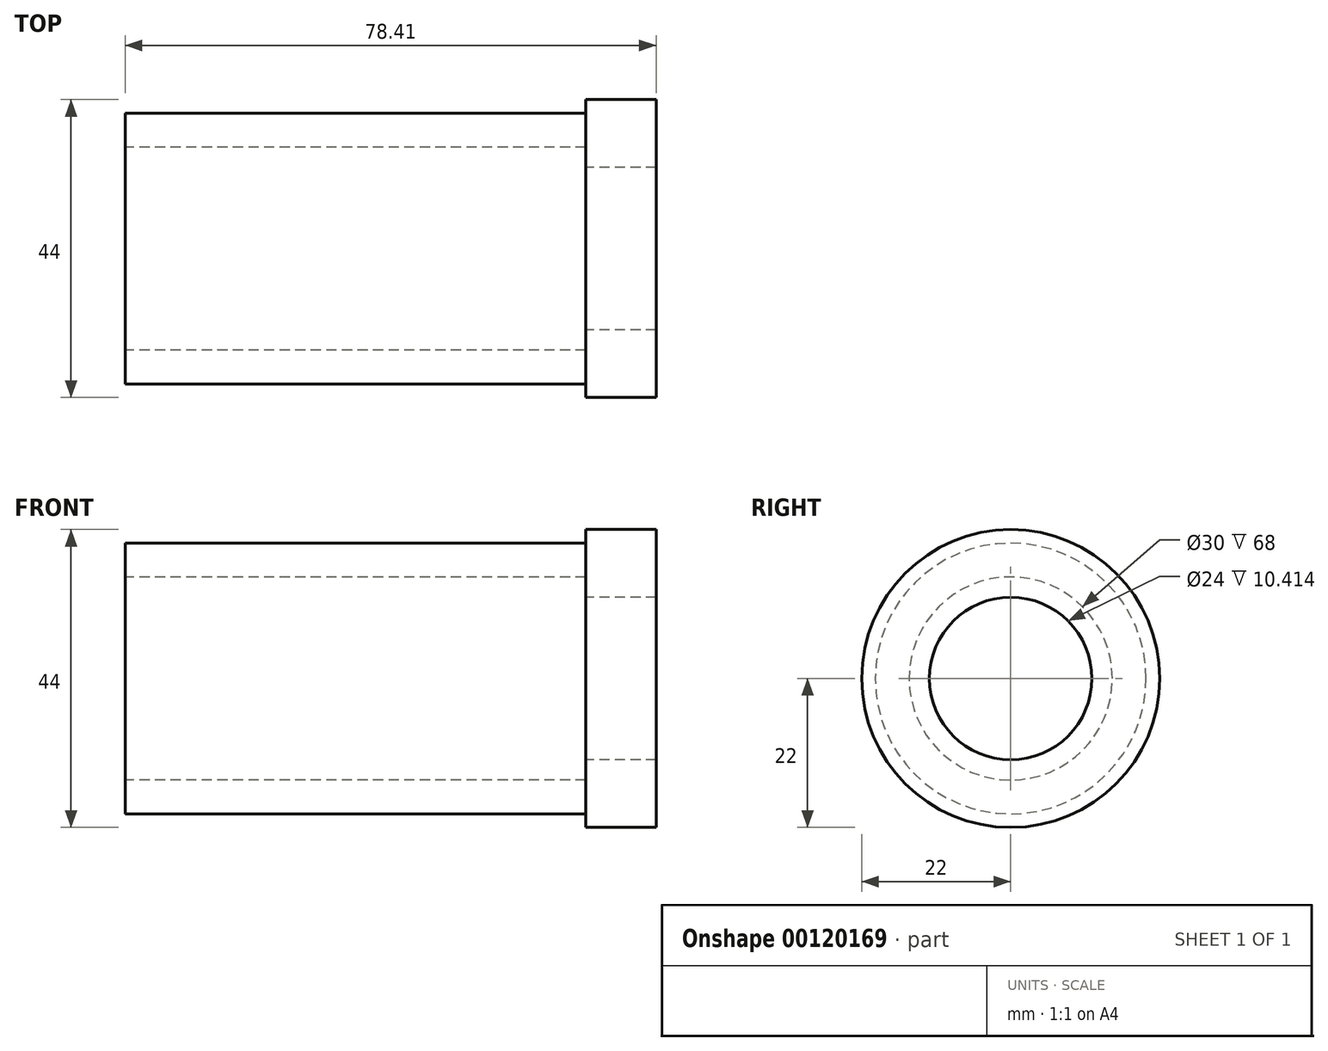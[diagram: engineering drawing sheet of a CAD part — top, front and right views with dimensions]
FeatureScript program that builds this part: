
annotation { "Feature Type Name" : "Feature", "Feature Type Description" : "" }
export const myFeature = defineFeature(function(context is Context, id is Id, definition is map)
    precondition{}
    {
        {
            var Q0;
            Q0=qCreatedBy(makeId("Right.planeOp"),FACE);
            var sketch = newSketch(context, id + "F0", { "sketchPlane" : qUnion([Q0])});
            skCircle(sketch, "E0", {"center": v(0, 0) * mm, "radius": 20 * mm});
            skCircle(sketch, "E1", {"center": v(0, 0) * mm, "radius": 15 * mm});
            skSolve(sketch);
        }
        {
            var Q0;
            Q0 = qSketchRegion(id + "F0", true);
            extrude(context, id + "F1", {"entities" : qUnion([Q0]), "endBound" : BoundingType.SYMMETRIC, "depth" : 68 * mm});
        }
        {
            var Q0;
            Q0=makeQuery(id+"F1.opExtrude","CAP_FACE",FACE,{"disambiguationData":[OSD([sQuery(id+"F0.wireOp",EDGE,"E0"),sQuery(id+"F0.wireOp",EDGE,"E1")])],"isStart":false});
            var sketch = newSketch(context, id + "F2", { "sketchPlane" : qUnion([Q0])});
            skCircle(sketch, "E2", {"center": v(0, 0) * mm, "radius": 12 * mm});
            skCircle(sketch, "E3", {"center": v(0, 0) * mm, "radius": 22 * mm});
            skSolve(sketch);
        }
        {
            var Q0;
            Q0 = qSketchRegion(id + "F2", true);
            extrude(context, id + "F3", {"entities" : qUnion([Q0]), "operationType" : NewBodyOperationType.ADD, "depth" : 10.4 * mm});
        }
    });
